# Revit family: AMY2_63_UN_Inlay LED_ETK
name_source: partatom
category: Lighting Fixtures
revit_build: Autodesk Revit 2017 (Build: 20190508_0315(x64)
units: mm (PartAtom-declared; Revit-internal decimal feet)

## family parameters
Always vertical = Yes
Cut with Voids When Loaded = No
Light Source = No
OmniClass Number = 23.80.70.11.14.11
OmniClass Title = Downlights
Part Type = Normal
Room Calculation Point = Yes
Round Connector Dimension = Use Diameter
Shared = No
Work Plane-Based = No

## types (8) — shared parameters
Assembly Code = 63.0
Bundle = 84°/87°
Description = Recessed/inlay LED
IfcExportAs = IfcLightFixtureType
IfcExportType = USERDEFINED
Lamp = LED
Luminaire_Body_Material = PPS Plastic
Manufacturer = ETK B.V.
Model = AMY.2
URL = https://www.etk.nl
Voltage = 230 V

## per-type parameters (varying)
| type | Apparent Load | Light Source | Wattage Comments |
| AMY.2100.15 - 22W / 3000lm / 3000K | 22 VA | AMY.2 - Lightsource : AMY.2100.15 - 22W / 3000lm / 3000K | 22W |
| AMY.2200.15 - 22W / 3100lm / 4000K | 22 VA | AMY.2 - Lightsource : AMY.2200.15 - 22W / 3100lm / 4000K | 22W |
| AMY.2300.15 - 31W / 4100lm / 3000K | 31 VA | AMY.2 - Lightsource : AMY.2300.15 - 31W / 4100lm / 3000K | 31W |
| AMY.2400.15 - 31W / 4250lm / 4000K | 31 VA | AMY.2 - Lightsource : AMY.2400.15 - 31W / 4250lm / 4000K | 31 |
| AMY.2103.15 - 22W / 3000lm / 3000K | 22 VA | AMY.2 - Lightsource : AMY.2103.15 - 22W / 3000lm / 3000K | 22W |
| AMY.2203.15 - 22W / 3100lm / 4000K | 22 VA | AMY.2 - Lightsource : AMY.2203.15 - 22W / 3100lm / 4000K | 22W |
| AMY.2303.15 - 31W / 4100lm / 3000K | 31 VA | AMY.2 - Lightsource : AMY.2303.15 - 31W / 4100lm / 3000K | 31W |
| AMY.2403.15 - 31W / 4250lm / 4000K | 31 VA | AMY.2 - Lightsource : AMY.2403.15 - 31W / 4250lm / 4000K | 31 |

## geometry (parser evidence)
native form markers: Sweep x7
no freeform markers — native parametric forms only
